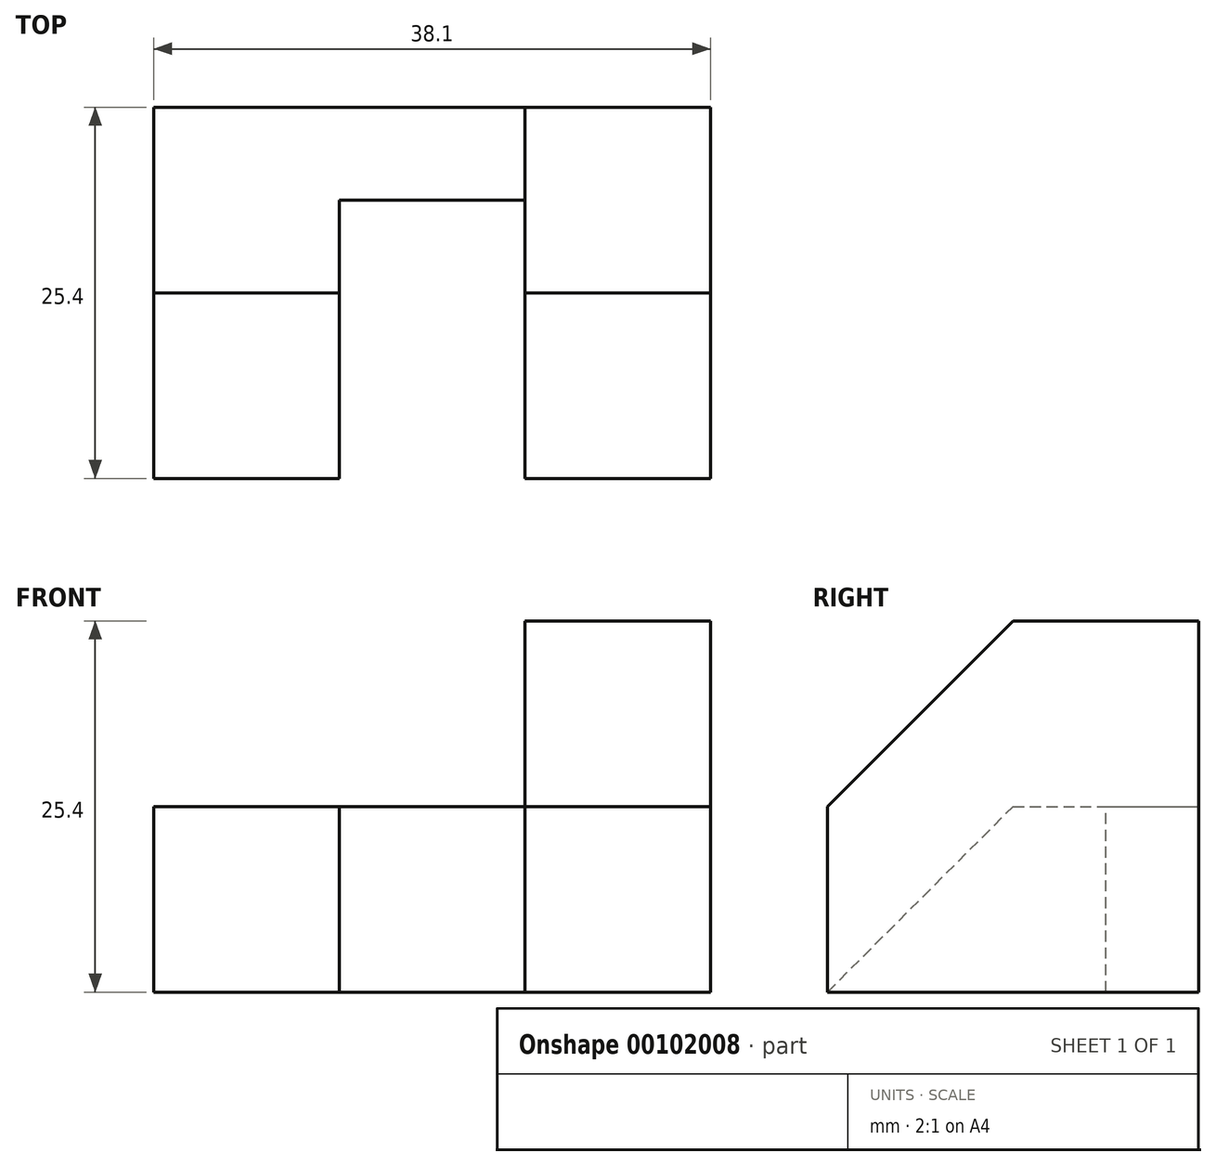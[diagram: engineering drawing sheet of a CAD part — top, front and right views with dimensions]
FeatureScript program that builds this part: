
annotation { "Feature Type Name" : "Feature", "Feature Type Description" : "" }
export const myFeature = defineFeature(function(context is Context, id is Id, definition is map)
    precondition{}
    {
        {
            var Q0;
            Q0=qCreatedBy(makeId("Front.planeOp"),FACE);
            var sketch = newSketch(context, id + "F0", { "sketchPlane" : qUnion([Q0])});
            skLineSegment(sketch, "E0", {"start": v(38.1, 0) * mm, "end": v(38.1, 25.4) * mm});
            skLineSegment(sketch, "E1", {"start": v(38.1, 25.4) * mm, "end": v(25.4, 25.4) * mm});
            skLineSegment(sketch, "E2", {"start": v(25.4, 25.4) * mm, "end": v(25.4, 0) * mm});
            skLineSegment(sketch, "E3", {"start": v(0, 0) * mm, "end": v(0, 12.7) * mm});
            skLineSegment(sketch, "E4", {"start": v(0, 12.7) * mm, "end": v(12.7, 12.7) * mm});
            skLineSegment(sketch, "E5", {"start": v(12.7, 12.7) * mm, "end": v(12.7, 0) * mm});
            skLineSegment(sketch, "E6", {"start": v(12.7, 0) * mm, "end": v(0, 0) * mm});
            skLineSegment(sketch, "E7", {"start": v(38.1, 0) * mm, "end": v(25.4, 0) * mm});
            skLineSegment(sketch, "E8", {"start": v(25.4, 0) * mm, "end": v(12.7, 0) * mm, "construction": true});
            skSolve(sketch);
        }
        {
            var Q0;
            Q0 = qSketchRegion(id + "F0", true);
            extrude(context, id + "F1", {"entities" : qUnion([Q0]), "depth" : 25.4 * mm});
        }
        {
            var Q0;
            Q0=qCreatedBy(makeId("Front.planeOp"),FACE);
            var sketch = newSketch(context, id + "F2", { "sketchPlane" : qUnion([Q0])});
            skLineSegment(sketch, "E9", {"start": v(0, 0) * mm, "end": v(12.7, 0) * mm, "construction": true});
            skLineSegment(sketch, "E10", {"start": v(12.7, 0) * mm, "end": v(25.4, 0) * mm});
            skLineSegment(sketch, "E11", {"start": v(25.4, 0) * mm, "end": v(25.4, 12.7) * mm});
            skLineSegment(sketch, "E12", {"start": v(25.4, 12.7) * mm, "end": v(12.7, 12.7) * mm});
            skLineSegment(sketch, "E13", {"start": v(12.7, 12.7) * mm, "end": v(12.7, 0) * mm});
            skSolve(sketch);
        }
        {
            var Q0;
            Q0 = qSketchRegion(id + "F2", true);
            extrude(context, id + "F3", {"entities" : qUnion([Q0]), "operationType" : NewBodyOperationType.ADD, "depth" : 6.35 * mm});
        }
        {
            var Q0;
            Q0=qCreatedBy(makeId("Right.planeOp"),FACE);
            var sketch = newSketch(context, id + "F4", { "sketchPlane" : qUnion([Q0])});
            skLineSegment(sketch, "E14", {"start": v(-12.7, 12.7) * mm, "end": v(-25.4, 12.7) * mm});
            skLineSegment(sketch, "E15", {"start": v(-25.4, 12.7) * mm, "end": v(-25.4, 0) * mm});
            skLineSegment(sketch, "E16", {"start": v(-25.4, 0) * mm, "end": v(-12.7, 12.7) * mm});
            skSolve(sketch);
        }
        {
            var Q0;
            Q0 = qSketchRegion(id + "F4", true);
            extrude(context, id + "F5", {"entities" : qUnion([Q0]), "operationType" : NewBodyOperationType.REMOVE, "depth" : 12.7 * mm});
        }
        {
            var Q0;
            Q0=qCreatedBy(makeId("Right.planeOp"),FACE);
            var sketch = newSketch(context, id + "F6", { "sketchPlane" : qUnion([Q0])});
            skLineSegment(sketch, "E17", {"start": v(-25.4, 25.4) * mm, "end": v(-12.7, 25.4) * mm});
            skLineSegment(sketch, "E18", {"start": v(-12.7, 25.4) * mm, "end": v(-25.4, 12.7) * mm});
            skLineSegment(sketch, "E19", {"start": v(-25.4, 12.7) * mm, "end": v(-25.4, 25.4) * mm});
            skSolve(sketch);
        }
        {
            var Q0;
            Q0 = qSketchRegion(id + "F6", true);
            extrude(context, id + "F7", {"entities" : qUnion([Q0]), "operationType" : NewBodyOperationType.REMOVE, "depth" : 38.1 * mm});
        }
    });
